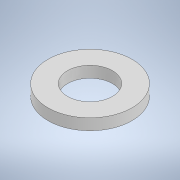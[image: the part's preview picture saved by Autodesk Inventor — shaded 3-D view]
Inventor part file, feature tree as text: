
AUTODESK INVENTOR PART (.ipt)
format: ipt  version: 2020.2 (Build 242310000, 310)  size: 98,304 bytes
history: native  units: mm
features: extrude x1, sketch x1
ambient origin geometry x8: Origin, YZ Plane, XZ Plane, XY Plane, X Axis, Y Axis, Z Axis, Center Point
bodies: Solido1 (feature_tree)
feature tree (2):
  extrude  "Estrusione1"  Depth=6.4mm
  sketch  "Schizzo1"
